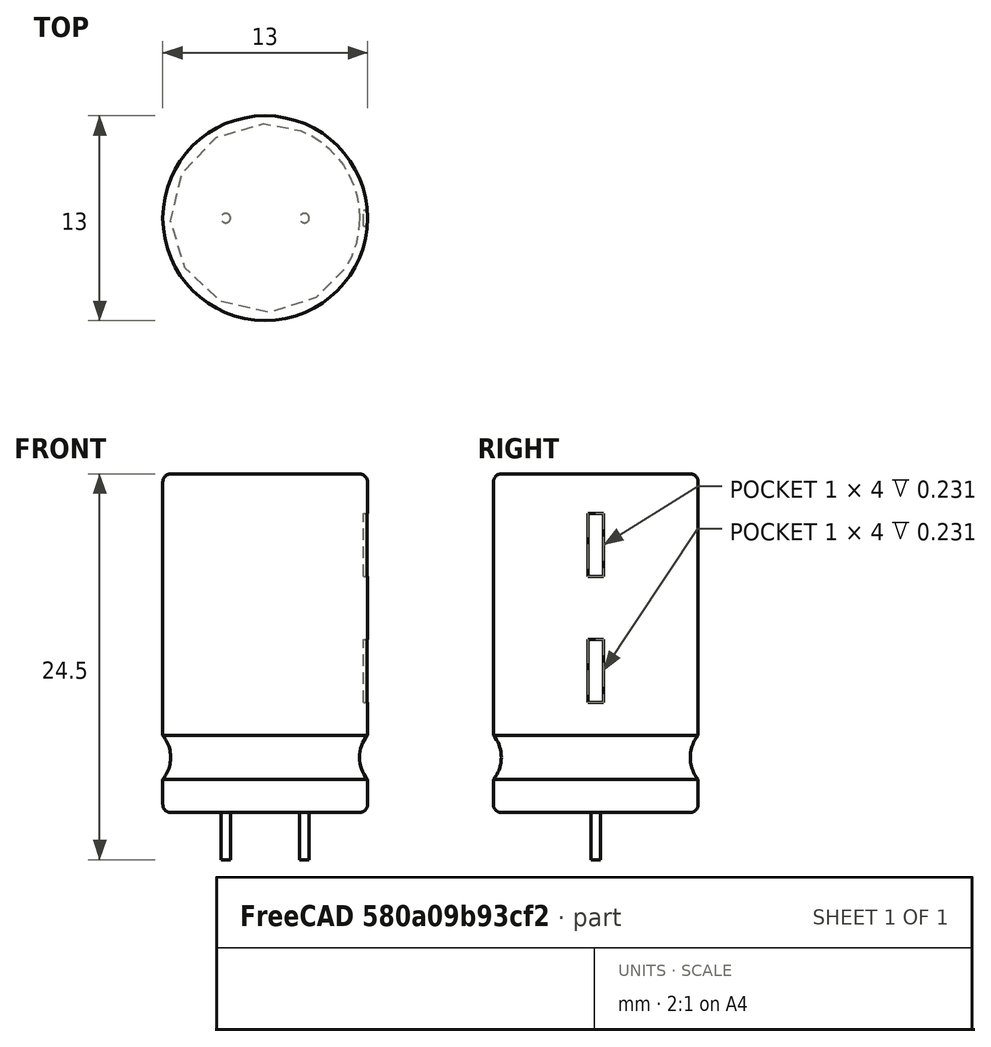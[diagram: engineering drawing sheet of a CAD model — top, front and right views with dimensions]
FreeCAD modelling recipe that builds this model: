
FCSTD DOCUMENT
Label: CAPPR500W60D1250H2000
objects: Part::Cylinder×3, Part::Cut×3, Part::Box×2, Part::Fuse×2, Part::Fillet×1, Part::Torus×1
note: 12 computed .brp shape members not serialized (recipe doc carries the construction recipe); baked Part::Feature solids carry a one-line shape summary decoded from their .brp

FEATURE [Part::Cylinder] Cylinder  label="Grundkoerper"
  Angle = 360
  Height = 21.5
  Radius = 6.5
FEATURE [Part::Cylinder] Cylinder001  label="Pin1+"
  Angle = 360
  Height = 3
  Placement = pos=(-2.5,0,-3) rot=(0,0,1;0rad)
  Radius = 0.3
FEATURE [Part::Cylinder] Cylinder002  label="Pin2-"
  Angle = 360
  Height = 3
  Placement = pos=(2.5,0,-3) rot=(0,0,1;0rad)
  Radius = 0.3
FEATURE [Part::Fillet] Fillet  label="Abgerundeter Grundkoerper"
  Base = -> Cylinder
  Edges = 2 edges r=0.5: [Edge1,Edge3]
FEATURE [Part::Torus] Torus  label="Ring"
  Angle1 = -180
  Angle2 = 180
  Angle3 = 360
  Placement = pos=(0,0,3.5) rot=(0,0,1;0rad)
  Radius1 = 8.2
  Radius2 = 2.2
FEATURE [Part::Cut] Cut  label="Beringter kondensator"
  Base = -> Fillet
  Tool = -> Torus
FEATURE [Part::Box] Box
  Height = 4
  Length = 1
  Placement = pos=(6.25,-0.5,7) rot=(0,0,1;0rad)
  Width = 1
FEATURE [Part::Box] Box001
  Height = 4
  Length = 1
  Placement = pos=(6.25,-0.5,15) rot=(0,0,1;0rad)
  Width = 1
FEATURE [Part::Cut] Cut001
  Base = -> Cut
  Tool = -> Box
FEATURE [Part::Cut] Cut002
  Base = -> Cut001
  Tool = -> Box001
FEATURE [Part::Fuse] Fusion
  Base = -> Cut002
  Tool = -> Cylinder001
FEATURE [Part::Fuse] Fusion001  label="CAPPR500W60D1250H2000"
  Base = -> Fusion
  Tool = -> Cylinder002
